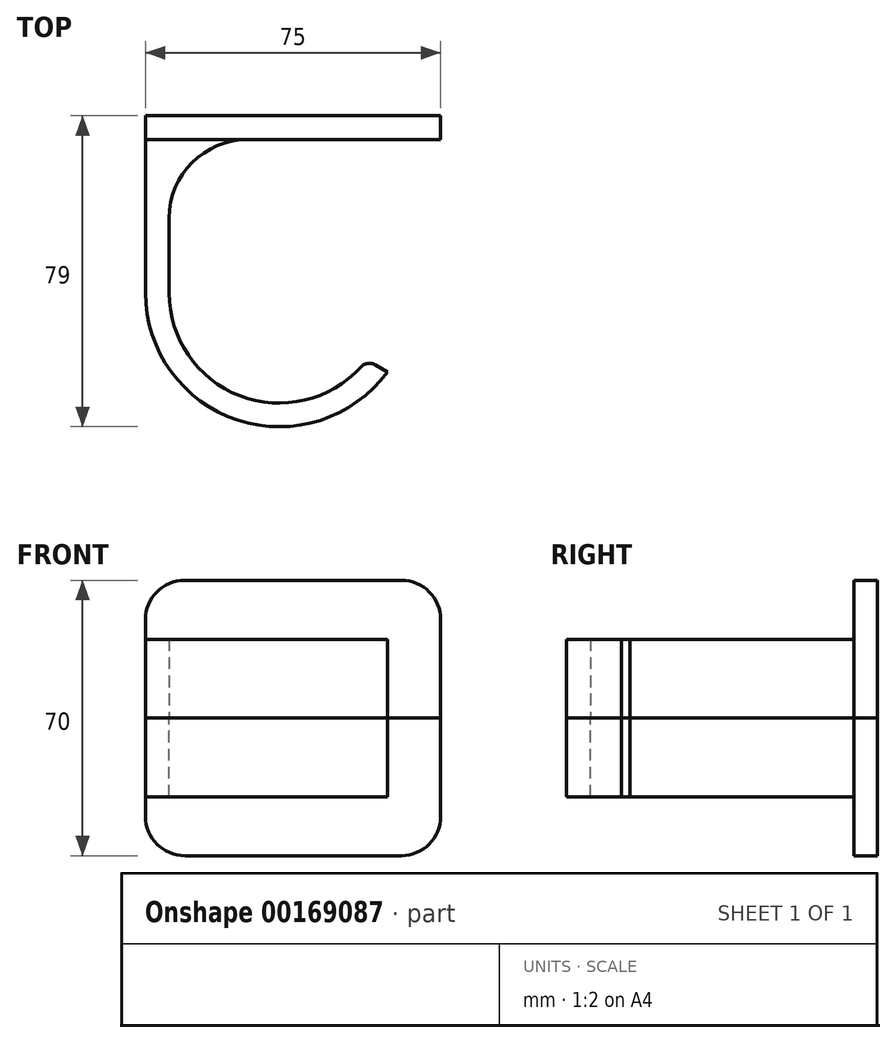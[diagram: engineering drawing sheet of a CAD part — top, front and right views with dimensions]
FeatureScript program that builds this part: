
annotation { "Feature Type Name" : "Feature", "Feature Type Description" : "" }
export const myFeature = defineFeature(function(context is Context, id is Id, definition is map)
    precondition{}
    {
        {
            var Q0;
            Q0=qCreatedBy(makeId("Top.planeOp"),FACE);
            var sketch = newSketch(context, id + "F0", { "sketchPlane" : qUnion([Q0])});
            skLineSegment(sketch, "E0", {"start": v(75, 0) * mm, "end": v(0, 0) * mm});
            skLineSegment(sketch, "E1", {"start": v(0, 0) * mm, "end": v(0, -45) * mm});
            skLineSegment(sketch, "E2", {"start": v(75, 0) * mm, "end": v(75, -6) * mm});
            skLineSegment(sketch, "E3", {"start": v(75, -6) * mm, "end": v(26, -6) * mm});
            skLineSegment(sketch, "E4", {"start": v(6, -26) * mm, "end": v(6, -45) * mm});
            skArc(sketch, "E5", {"start": v(6, -45) * mm, "mid": v(25.03, -71.52) * mm, "end": v(56.25, -62) * mm});
            skArc(sketch, "E6.0", {"start": v(0, -45) * mm, "mid": v(23.44, -77.32) * mm, "end": v(61.44, -65.08) * mm});
            skLineSegment(sketch, "E7", {"start": v(56.25, -62) * mm, "end": v(61.44, -65.08) * mm});
            skLineSegment(sketch, "E8", {"start": v(6, -45) * mm, "end": v(34, -45) * mm});
            skLineSegment(sketch, "E9", {"start": v(34, -79) * mm, "end": v(62.8, -79) * mm});
            skPoint(sketch, "E10.visualSharp", {"position": v(6, -6) * mm});
            skArc(sketch, "E10.filletArc", {"start": v(26, -6) * mm, "mid": v(11.86, -11.86) * mm, "end": v(6, -26) * mm});
            skSolve(sketch);
        }
        {
            var Q0;
            Q0 = qSketchRegion(id + "F0", true);
            extrude(context, id + "F1", {"entities" : qUnion([Q0]), "depth" : 20 * mm});
        }
        {
            var Q0;
            Q0=makeQuery(id+"F1.opExtrude","CAP_FACE",FACE,{"disambiguationData":[OSD([sQuery(id+"F0.wireOp",EDGE,"E0"),sQuery(id+"F0.wireOp",EDGE,"E1"),sQuery(id+"F0.wireOp",EDGE,"E2"),sQuery(id+"F0.wireOp",EDGE,"E3"),sQuery(id+"F0.wireOp",EDGE,"E4"),sQuery(id+"F0.wireOp",EDGE,"E5"),sQuery(id+"F0.wireOp",EDGE,"E6.0"),sQuery(id+"F0.wireOp",EDGE,"E7")])],"isStart":false});
            var sketch = newSketch(context, id + "F2", { "sketchPlane" : qUnion([Q0])});
            skLineSegment(sketch, "E11.bottom", {"start": v(0, 0) * mm, "end": v(75, 0) * mm});
            skLineSegment(sketch, "E11.top", {"start": v(0, -6) * mm, "end": v(75, -6) * mm});
            skLineSegment(sketch, "E11.left", {"start": v(0, 0) * mm, "end": v(0, -6) * mm});
            skLineSegment(sketch, "E11.right", {"start": v(75, 0) * mm, "end": v(75, -6) * mm});
            skSolve(sketch);
        }
        {
            var Q0;
            Q0 = qSketchRegion(id + "F2", true);
            extrude(context, id + "F3", {"entities" : qUnion([Q0]), "operationType" : NewBodyOperationType.ADD, "depth" : 15 * mm});
        }
        {
            var Q0;
            Q0=makeQuery(id+"F1.opExtrude","SWEPT_EDGE",EDGE,{"disambiguationData":[OSD([sQuery(id+"F0.wireOp",EDGE,"E5"),sQuery(id+"F0.wireOp",EDGE,"E7")])]});
            fillet(context, id + "F4", {"entities" : qUnion([Q0]), "radius" : 3 * mm, "tangentPropagation" : true, "allowEdgeOverflow" : false});
        }
        {
            var Q0;
            Q0=makeQuery(id+"F3.opExtrude","CAP_EDGE",EDGE,{"disambiguationData":[OSD([sQuery(id+"F2.wireOp",EDGE,"E11.left")])],"isStart":false});
            var Q1;
            Q1=makeQuery(id+"F3.opExtrude","CAP_EDGE",EDGE,{"disambiguationData":[OSD([sQuery(id+"F2.wireOp",EDGE,"E11.right")])],"isStart":false});
            fillet(context, id + "F5", {"entities" : qUnion([Q0, Q1]), "radius" : 10 * mm, "tangentPropagation" : true, "allowEdgeOverflow" : false});
        }
        {
            var Q0;
            Q0=makeQuery(id+"F1.opExtrude","SWEPT_BODY",BODY,{"disambiguationData":[OSD([sQuery(id+"F0.wireOp",EDGE,"E0"),sQuery(id+"F0.wireOp",EDGE,"E1"),sQuery(id+"F0.wireOp",EDGE,"E2"),sQuery(id+"F0.wireOp",EDGE,"E3"),sQuery(id+"F0.wireOp",EDGE,"E4"),sQuery(id+"F0.wireOp",EDGE,"E5"),sQuery(id+"F0.wireOp",EDGE,"E6.0"),sQuery(id+"F0.wireOp",EDGE,"E7"),sQuery(id+"F0.wireOp",EDGE,"E10.filletArc")])]});
            var Q1;
            Q1=qCreatedBy(makeId("Top.planeOp"),FACE);
            mirror(context, id + "F6", {"entities" : qUnion([Q0]), "mirrorPlane" : qUnion([Q1])});
        }
    });
